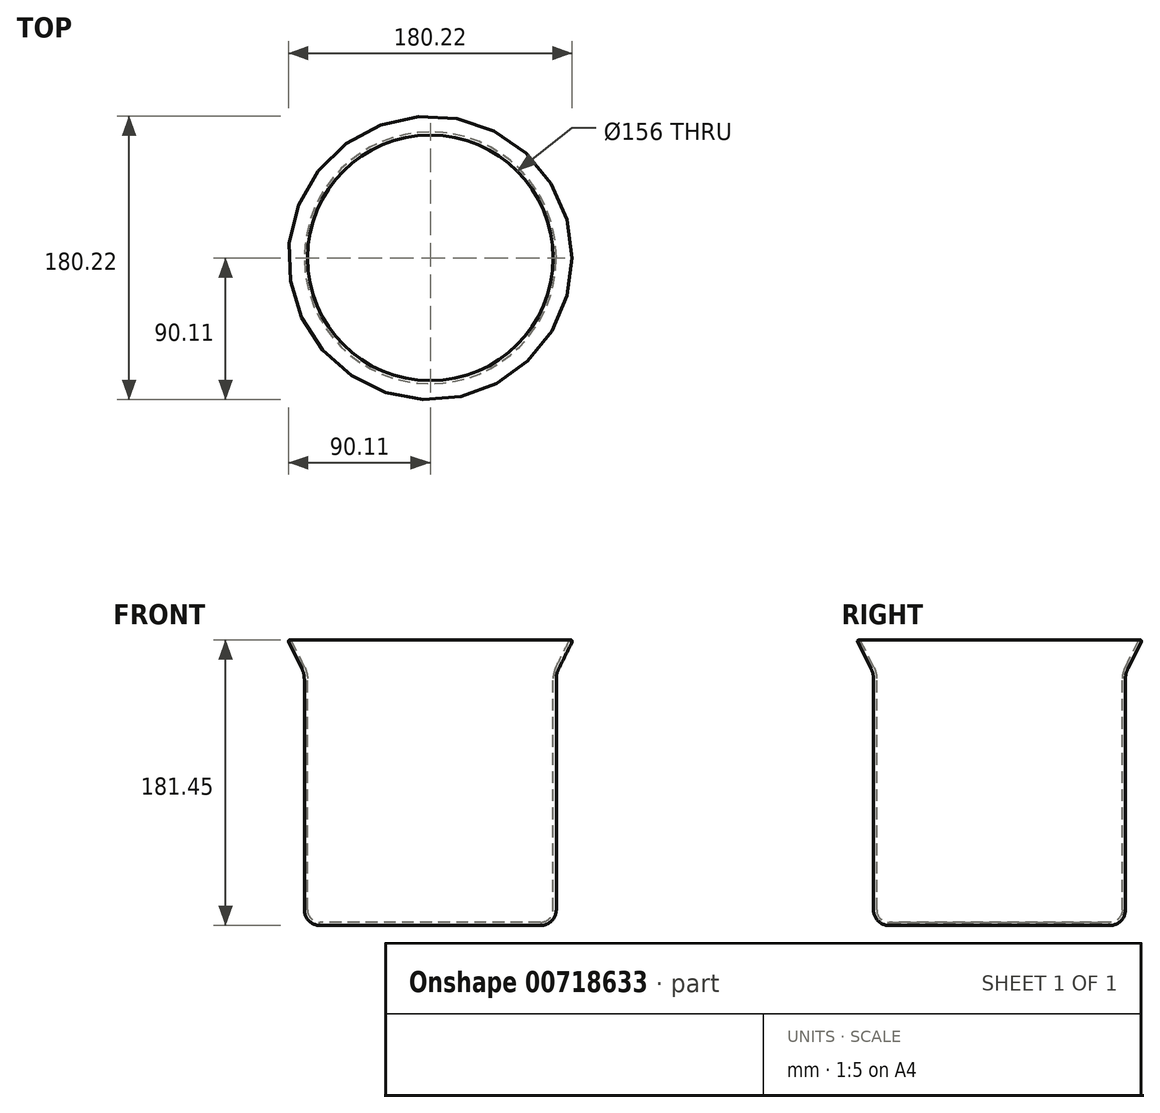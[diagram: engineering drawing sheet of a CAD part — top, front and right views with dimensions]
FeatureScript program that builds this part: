
annotation { "Feature Type Name" : "Feature", "Feature Type Description" : "" }
export const myFeature = defineFeature(function(context is Context, id is Id, definition is map)
    precondition{}
    {
        {
            var Q0;
            Q0=qCreatedBy(makeId("Right.planeOp"),FACE);
            var sketch = newSketch(context, id + "F0", { "sketchPlane" : qUnion([Q0])});
            skLineSegment(sketch, "E0", {"start": v(0, -13.65) * mm, "end": v(0, 96.9) * mm, "construction": true});
            skLineSegment(sketch, "E1", {"start": v(0, 0) * mm, "end": v(-70, 0) * mm});
            skLineSegment(sketch, "E2", {"start": v(-80, 10) * mm, "end": v(-80, 156.46) * mm});
            skLineSegment(sketch, "E3", {"start": v(-81.58, 163.17) * mm, "end": v(-90, 180) * mm});
            skPoint(sketch, "E4.visualSharp", {"position": v(-80, 160) * mm});
            skArc(sketch, "E4.filletArc", {"start": v(-80, 156.46) * mm, "mid": v(-80.4, 159.9) * mm, "end": v(-81.58, 163.17) * mm});
            skPoint(sketch, "E5.visualSharp", {"position": v(-80, 0) * mm});
            skArc(sketch, "E5.filletArc", {"start": v(-80, 10) * mm, "mid": v(-77.07, 2.93) * mm, "end": v(-70, 0) * mm});
            skLineSegment(sketch, "E6.0", {"start": v(-79.8, 164.06) * mm, "end": v(-88.21, 180.9) * mm});
            skLineSegment(sketch, "E6.1", {"start": v(0, 2) * mm, "end": v(-70, 2) * mm});
            skArc(sketch, "E6.2", {"start": v(-78, 10) * mm, "mid": v(-75.66, 4.34) * mm, "end": v(-70, 2) * mm});
            skLineSegment(sketch, "E6.3", {"start": v(-78, 10) * mm, "end": v(-78, 156.46) * mm});
            skArc(sketch, "E6.4", {"start": v(-78, 156.46) * mm, "mid": v(-78.45, 160.36) * mm, "end": v(-79.8, 164.06) * mm});
            skArc(sketch, "E7", {"start": v(-88.21, 180.9) * mm, "mid": v(-89.55, 181.34) * mm, "end": v(-90, 180) * mm});
            skLineSegment(sketch, "E8", {"start": v(0, 2) * mm, "end": v(0, 0) * mm});
            skSolve(sketch);
        }
        {
            var Q0;
            Q0=makeQuery(id+"F0.imprint","IMPRINT",FACE,{"disambiguationData":[TD([[makeQuery(id+"F0.imprint","IMPRINT",EDGE,{"derivedFrom":sQuery(id+"F0.wireOp",EDGE,"E1")}),-1.0]])]});
            var Q1;
            Q1=sQuery(id+"F0.wireOp",EDGE,"E0");
            revolve(context, id + "F1", {"entities" : qUnion([Q0]), "axis" : qUnion([Q1]), "revolveType" : RevolveType.FULL, "oppositeDirection" : true});
        }
    });
